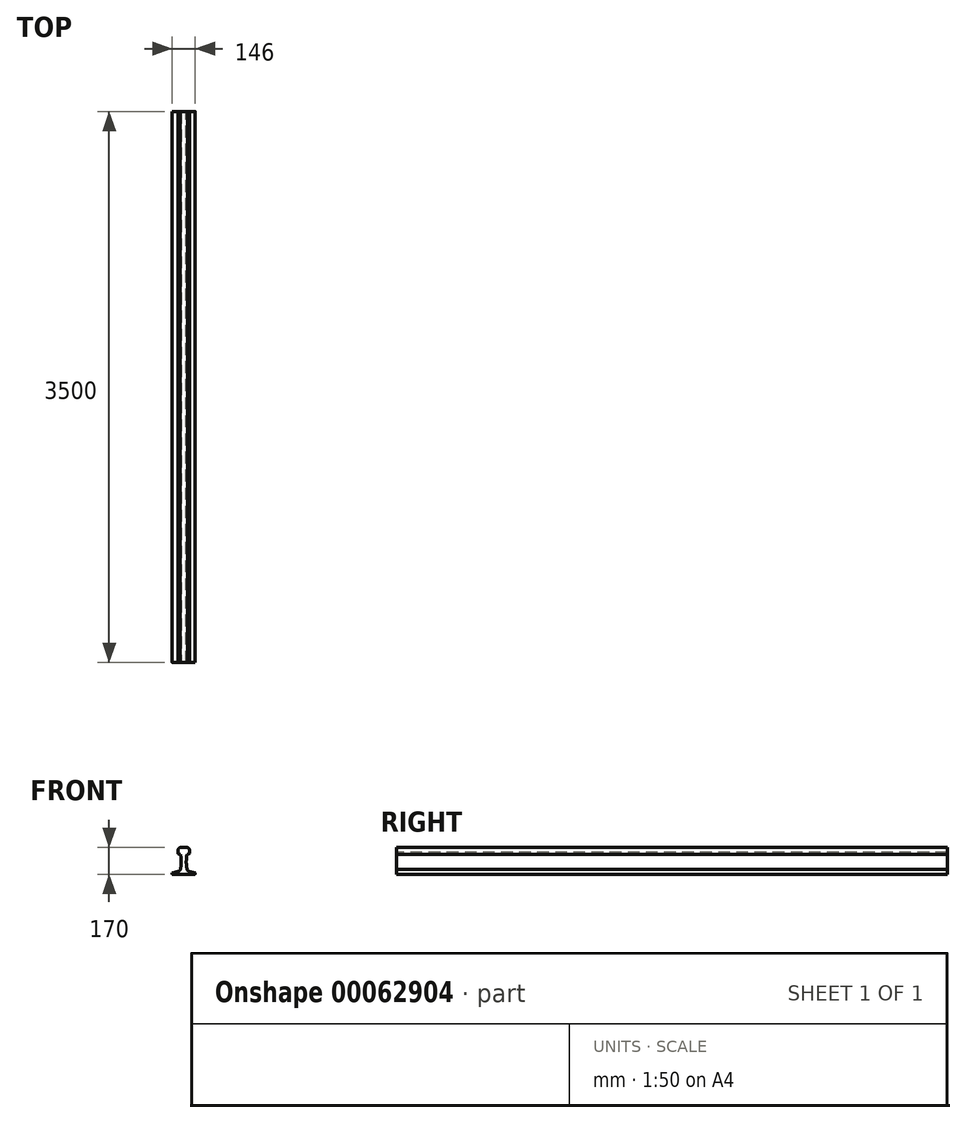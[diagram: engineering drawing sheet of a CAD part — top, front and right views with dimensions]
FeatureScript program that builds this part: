
annotation { "Feature Type Name" : "Feature", "Feature Type Description" : "" }
export const myFeature = defineFeature(function(context is Context, id is Id, definition is map)
    precondition{}
    {
        {
            var Q0;
            Q0=qCreatedBy(makeId("Front.planeOp"),FACE);
            var sketch = newSketch(context, id + "F0", { "sketchPlane" : qUnion([Q0])});
            skLineSegment(sketch, "E0", {"start": v(0, 0) * mm, "end": v(71, 0) * mm});
            skLineSegment(sketch, "E1", {"start": v(0, 0) * mm, "end": v(-71, 0) * mm});
            skLineSegment(sketch, "E2", {"start": v(0, 0) * mm, "end": v(0, 170) * mm, "construction": true});
            skLineSegment(sketch, "E3", {"start": v(-73, 2) * mm, "end": v(-73, 7.4) * mm});
            skArc(sketch, "E4", {"start": v(-73, 2) * mm, "mid": v(-72.41, 0.59) * mm, "end": v(-71, 0) * mm});
            skArc(sketch, "E5", {"start": v(-70.73, 10.32) * mm, "mid": v(-72.36, 9.25) * mm, "end": v(-73, 7.4) * mm});
            skLineSegment(sketch, "E6", {"start": v(73, 2) * mm, "end": v(73, 7.4) * mm});
            skArc(sketch, "E7", {"start": v(71, 0) * mm, "mid": v(72.41, 0.59) * mm, "end": v(73, 2) * mm});
            skArc(sketch, "E8", {"start": v(73, 7.4) * mm, "mid": v(72.36, 9.25) * mm, "end": v(70.73, 10.32) * mm});
            skLineSegment(sketch, "E9", {"start": v(0, 170) * mm, "end": v(-24.05, 170) * mm});
            skLineSegment(sketch, "E10", {"start": v(-35.76, 154.84) * mm, "end": v(-36.44, 141.14) * mm});
            skLineSegment(sketch, "E11.bottom", {"start": v(-24.05, 170) * mm, "end": v(-19, 170) * mm});
            skArc(sketch, "E12", {"start": v(-24.05, 170) * mm, "mid": v(-32.28, 164.25) * mm, "end": v(-35.76, 154.84) * mm});
            skLineSegment(sketch, "E13", {"start": v(-20.05, 126.01) * mm, "end": v(-27.21, 127.8) * mm});
            skLineSegment(sketch, "E14", {"start": v(-36.44, 141.14) * mm, "end": v(-36.56, 138.8) * mm});
            skFitSpline(sketch, "E15", {"points": [v(-36.44, 141.14) * mm, v(-35.26, 131.7) * mm, v(-27.21, 127.8) * mm], "startDerivative": vector(-1.23, -21.29) * mm, "endDerivative": vector(19.8, -5.3) * mm});
            skArc(sketch, "E16", {"start": v(-34.7, 19.32) * mm, "mid": v(-25.9, 24.11) * mm, "end": v(-20.53, 32.58) * mm});
            skLineSegment(sketch, "E17.trimOffspring", {"start": v(-34.7, 19.32) * mm, "end": v(-70.73, 10.32) * mm});
            skPoint(sketch, "E18.orphan", {"position": v(-20.48, 32.71) * mm});
            skPoint(sketch, "E19.end.orphan", {"position": v(-20.48, 32.58) * mm});
            skFitSpline(sketch, "E20", {"points": [v(-20.53, 32.58) * mm, v(-16.85, 65.47) * mm, v(-16.62, 88.53) * mm, v(-18.01, 110.11) * mm, v(-19.64, 123.31) * mm, v(-20.05, 126.01) * mm], "startDerivative": vector(15, 122.65) * mm, "endDerivative": vector(-2.95, 27.62) * mm});
            skLineSegment(sketch, "E21.MirrorCS", {"start": v(0, 170) * mm, "end": v(24.05, 170) * mm});
            skArc(sketch, "E22.MirrorCS", {"start": v(24.05, 170) * mm, "mid": v(32.28, 164.25) * mm, "end": v(35.76, 154.84) * mm});
            skLineSegment(sketch, "E23.MirrorCS", {"start": v(35.76, 154.84) * mm, "end": v(36.44, 141.14) * mm});
            skFitSpline(sketch, "E24.MirrorCS", {"points": [v(36.44, 141.14) * mm, v(35.26, 131.7) * mm, v(27.21, 127.8) * mm], "startDerivative": vector(1.23, -21.29) * mm, "endDerivative": vector(-19.8, -5.3) * mm});
            skLineSegment(sketch, "E25.MirrorCS", {"start": v(20.05, 126.01) * mm, "end": v(27.21, 127.8) * mm});
            skFitSpline(sketch, "E26.MirrorCS", {"points": [v(20.53, 32.58) * mm, v(16.85, 65.47) * mm, v(16.62, 88.53) * mm, v(18.01, 110.11) * mm, v(19.64, 123.31) * mm, v(20.05, 126.01) * mm], "startDerivative": vector(-15, 122.65) * mm, "endDerivative": vector(2.95, 27.62) * mm});
            skArc(sketch, "E27.MirrorCS", {"start": v(34.7, 19.32) * mm, "mid": v(25.9, 24.11) * mm, "end": v(20.53, 32.58) * mm});
            skLineSegment(sketch, "E28.MirrorCS", {"start": v(34.7, 19.32) * mm, "end": v(70.73, 10.32) * mm});
            skSolve(sketch);
        }
        {
            var Q0;
            Q0=qSketchRegion(id+"F0",true);
            extrude(context, id + "F1", {"entities" : qUnion([Q0]), "depth" : 3500 * mm});
        }
    });
